# Revit family: 2019_ES_Ventana_QSystems_Q87HO_2-Hojas
name_source: partatom
category: Windows
units: mm (PartAtom-declared; Revit-internal decimal feet)

## family parameters
Always vertical = Yes
Cut with Voids When Loaded = No
Host = Wall
OmniClass Number = 23.30.20.00
OmniClass Title = Windows
Room Calculation Point = No
Shared = No

## types (4) — shared parameters
Abatible = No
Acabado = Anodizado, lacado y acabados
Acristalamiento = Cristal - Vidrio claro templado
Altura Real = 1480.000 mm
Altura de antepecho por defecto = 500.000 mm
Altura maxima = 2500.000 mm
Altura minima = 600.000 mm
Analytic Construction = 1/4 in Pilkington single glazing
AnchoMarcoCentral = 111.400 mm
AnchoMarcoPerimetral = 74.100 mm
AnchoPoliamidaHoja = 37.400 mm
AnchoPoliamidaMarco = 34.000 mm
Anchura Maxima = 1700.000 mm
Anchura Minima = 100.000 mm
Anchura Real = 1230.000 mm
Area = 1.820 m²
Autor = Bimetica Parametric Design Services, S.L.
BIMsupport = https://bimsupport.info
Bimetica = http://www.bimetica.com
COBieCategoria = IfcWindow
Catálogo (URL) = https://qsystemsaluminio.com
CerramientoExterior = Yes
Clasificacion acustica = 45 (-2,-6) dB
ConfiguracionPoliamidas = 506400 - 268400 - 429300
ControlHumos = No
CosteEnergeticoMj = 0 J
EspesorPerfilesAluminio = 1.500 mm
EstanqueidadAgua = E1200
FechaEmisionElementoBIM = 03/12/2021
FechaVencimientoElementoBIM = 03/12/2022
FraccionAreaAcristalamiento = 70.99%
GrosorAcristalamiento = 42.000 mm
GrosorAcristalamiento Real = 42.000 mm
GrosorHoja = 80.000 mm
GrosorMarco = 80.000 mm
GrosorMaximoAcristalamiento = 42.000 mm
GrosorMinimoAcristalamiento = 0.000 mm
Gubimclass Codigo = 30.10.20.10
Gubimclass Titulo = Ventanas de fachadas
Heat Transfer Coefficient (U) = 6.7018 W/(m²·K)
Height = 1480.000 mm
Historial = (RVT2019) Actualziación a estándar GDO-BIM y datos. (RVT2015) Creación del Elemento.
IfcExportAs = IfcWindow
InformacionTecnica = https://qsystemsaluminio.com
Intercalario = Technoform Warm Edge
Manija = Yes
Manufacturer = QSystems
Marcado CE = No
Marco = Aluminio Anodizado, lacado
MasterformatCodigo = 08 50 00
MasterformatTitulo = Windows
Motorizada = No
Numero de Licencia = XXX-XXXX9536
OmniclassCodigo = 23-17 13 00
OmniclassTitulo = Windows
Perimetro = 5420
PermeabilidadAlAire = Clase 4
Peso = 0.00 kg
PesoMáximoDeLaHoja = 0.00 kg
Plataforma descaga contenido BIM = www.bimetica.com
Poliamida = Technoform polyamide
Porcentaje materiales reciclados = 0.00%
Profundidad = 0.000 mm
PuntoDeContacto = QSystems
Referencia = Q87HO
ReferenciaContacto = QSystems
RepisaExterior = Yes
RepisaInterior = Yes
SalidaEmergencia = No
Serie = Q87HO
Solar Heat Gain Coefficient = 0.86
TelefonoContacto = +34 91 895 58 00
Thermal Resistance (R) = 0.1492 (m²·K)/W
Titular = Alueuropa S.A.
Total Y𝑔 = 0.11
Total 𝐴𝑓 = 0.528021
Total 𝐴𝑔 = 1.292379
Total 𝑈𝑔 = 1.2
Total 𝑙𝑔 = 7.268
UNSPSCCodigo = 30171600
UNSPSCTitulo = Windows
URL = http://qsystemsaluminio.com
URL Perfil BIM = https://bimetica.com
URL Poliamida = http://www.technoform.es
URL Poliamida - Catálogo = http://www.technoform.com
URLProducto = https://qsystemsaluminio.com
Uniclass2.0Codigo = Ss_15_50_25
Uniclass2.0Titulo = Doors, Windows And Glazing Survey Systems
Version = RVT2019
Version Estandar GDO-BIM = GDO-BIM V02
Visual Light Transmittance = 0.9
Wall Closure = By host
Width = 1230.000 mm
Y𝑔 P1 = 0.11
Y𝑔 P2 = 0.11
𝐴𝑓 P1 = 0.380 m²
𝐴𝑓 P2 = 0.148 m²
𝐴𝑔 V1 = 0.646 m²
𝐴𝑔 V2 = 0.646 m²
𝑈𝑔 V1 = 1.2
𝑈𝑔 V2 = 1.2
𝑙𝑔 P1 = 4.6044
𝑙𝑔 P2 = 2.6636
zero-valued in all types: AcidificacionAtmosferica, AcidificacionAtmosfericaPorUnidad, AguaConsumida, AguaConsumidaPorUnidad, CambioClimatico, CambioClimaticoPorUnidad, CosteEnergeticoKwh, CosteMantenimiento, DestruccionCapaOzonoEstratosferica, DestruccionCapaOzonoEstratosfericaPorUnidad, EmisionCO2, Energia consumida, EnergiaNoRenovableConsumida, EnergiaNoRenovableConsumidaPorUnidad, EnergiaPrimariaTotalConsumida, EnergiaPrimariaTotalConsumidaPorUnidad, EnergiaRenovableConsumida, EnergiaRenovableConsumidaPorUnidad, Eutrofizacion, EutrofizacionPorUnidad, FactorSolarModificado, FactorSombra, FaltaDeRecursos, FaltaDeRecursosPorUnidad, FormacionFotoquimicaOzono, FormacionFotoquimicaOzonoPorUnidad, Fraccion de area de acristalamiento, Infiltracion, MasaSuperficialKgm2, ResiduoInerte, ResiduoInertePorUnidad, ResiduoRadioactivo, ResiduoRadioactivoPorUnidad, ResiduosNoPeligrosos, ResiduosNoPeligrososPorUnidad, ResiduosPeligrosos, ResiduosPeligrososPorUnidad, Transmitancia termica

## per-type parameters (varying)
| type | Description | Espuma | IfcExportType | Model | Operation | Oscilobatiente | Practicable | ResistenciaAlViento | Total 𝑈𝑓 | TransmitanciaTermica | 𝑈𝑓 P1 | 𝑈𝑓 P2 | 𝑈𝑤 |
| 1230x1480 mm - Practicable | Ventana 2 Hojas Practicables Q87HO de QSystems |  | Practicable | VentanaQ87HO - 2 Hojas Practicable | Practicable. Ventana Practicable de dos hojas con apertura Interior | No | Yes |  | 2.171902 | 1.9211 W/(m²·K) | 2.2 | 2.1 | 1.921086 |
| 1230x1480 mm - Oscilobatiente | Ventana 2 Hojas Oscilobatientes  Q87HO de QSystems |  | Oscilobatiente | VentanaQ87HO - 2 Hojas Oscilobatiente | Oscilobatiente. Ventana Oscilobatiente de dos hojas con apertura Interior | Yes | No | Clase C5 | 2.171902 | 1.9211 W/(m²·K) | 2.2 | 2.1 | 1.921086 |
| 1230x1480 mm - Oscilobatiente Con Espuma | Ventana 2 Hojas Oscilobatientes  Q87HO de QSystems con espuma | Espuma de conductividad 0.021W/mK entre varillas.
Espuma de conductividad 0.034W/mK en el galce del vidrio y en el marco. | Oscilobatiente | VentanaQ87HO - 2 Hojas Oscilobatiente con Espuma | Oscilobatiente. Ventana Oscilobatiente de dos hojas con apertura Interior | Yes | No | Clase C5 | 1.771902 | 1.8051 W/(m²·K) | 1.8 | 1.7 | 1.805063 |
| 1230x1480 mm - Practicable Con Espuma | Ventana 2 Hojas Practicables Q87HO de QSystems con espuma | Espuma de conductividad 0.021W/mK entre varillas.
Espuma de conductividad 0.034W/mK en el galce del vidrio y en el marco. | Practicable | VentanaQ87HO - 2 Hojas Practicable con Espuma | Practicable. Ventana Practicable de dos hojas con apertura Interior | No | Yes |  | 1.771902 | 1.8051 W/(m²·K) | 1.8 | 1.7 | 1.805063 |

## geometry (parser evidence)
native form markers: Blend x2
no freeform markers — native parametric forms only
